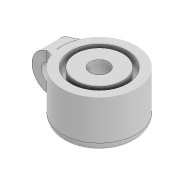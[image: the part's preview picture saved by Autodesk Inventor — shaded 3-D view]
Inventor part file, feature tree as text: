
AUTODESK INVENTOR PART (.ipt)
format: ipt  version: 2022 (Build 260153000, 153)  size: 167,424 bytes
history: native  units: mm
features: extrude x3, sketch x3, projected_geometry x2, fillet x1
ambient origin geometry x8: Origin, YZ Plane, XZ Plane, XY Plane, X Axis, Y Axis, Z Axis, Center Point
bodies: Solid1 (feature_tree)
feature tree (9):
  extrude  "Extrusion1"  Depth=2.5mm TaperAngle=0.0deg
  extrude  "Extrusion2"  Depth=12.2mm
  extrude  "Extrusion3"  Depth=2.0mm
  fillet  "Fillet2"  Radius=5.0mm
  sketch  "Sketch1"  dims[d0=16.0mm d1=2.5mm d2=0.0mm]
  sketch  "Sketch2"  dims[d3=10.2mm d4=12.2mm]
  projected_geometry  "Projected Loop1"
  sketch  "Sketch3"  dims[d5=8.0mm d6=0.0mm d8=4.0mm d11=5.0mm d12=0.0mm d14=4.0mm d15=2.0mm d16=4.0mm d17=2.0mm]
  projected_geometry  "Projected Loop2"
